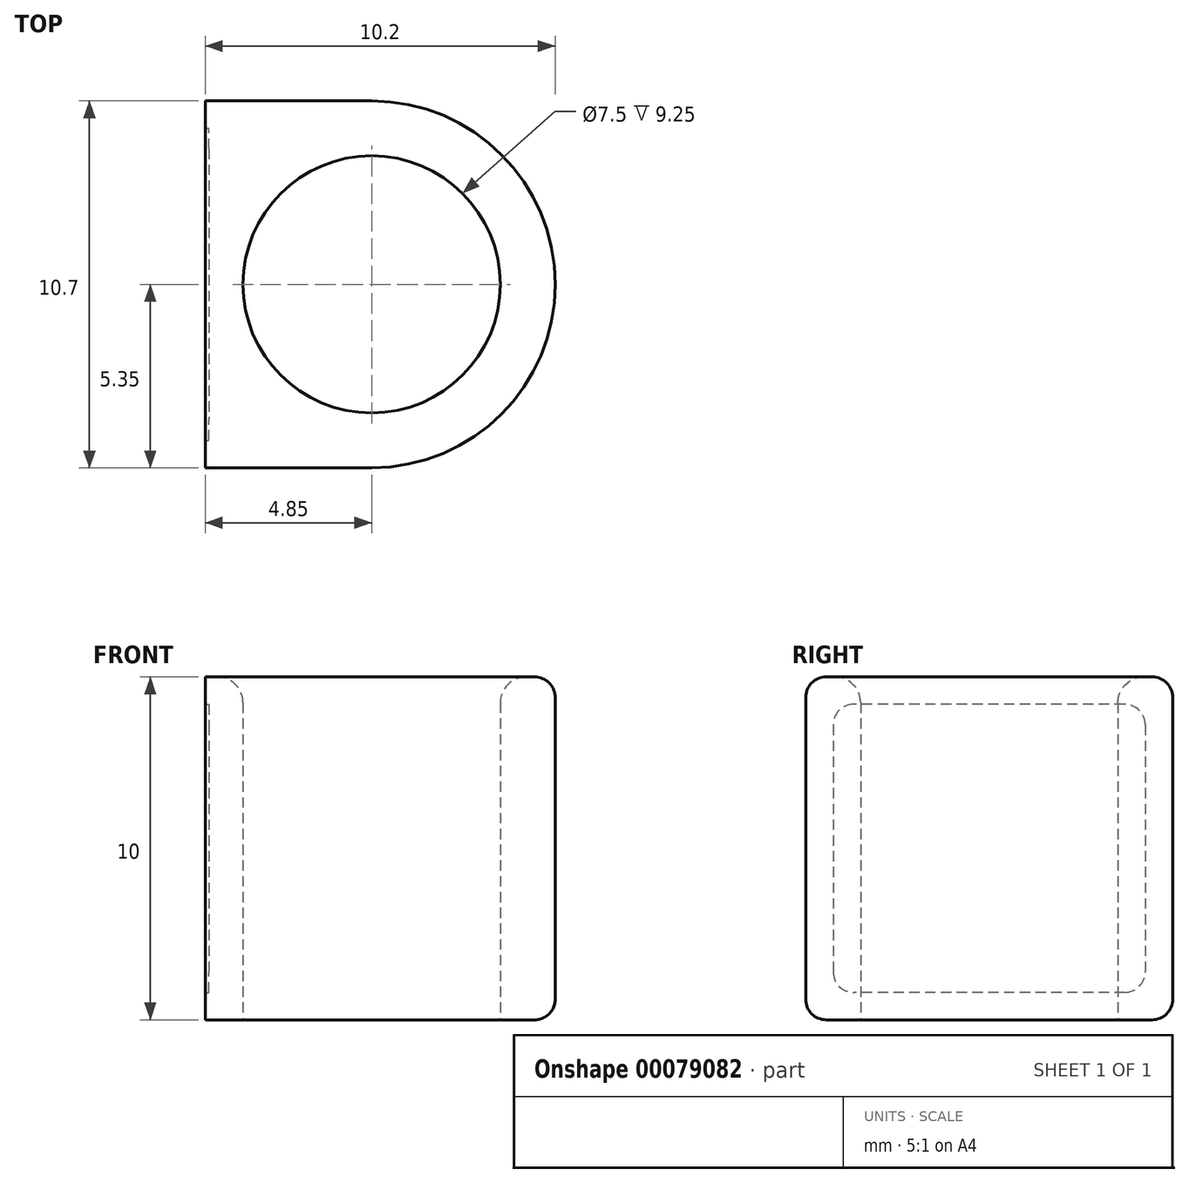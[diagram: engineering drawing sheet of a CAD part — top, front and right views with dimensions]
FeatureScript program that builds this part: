
annotation { "Feature Type Name" : "Feature", "Feature Type Description" : "" }
export const myFeature = defineFeature(function(context is Context, id is Id, definition is map)
    precondition{}
    {
        {
            var Q0;
            Q0=qCreatedBy(makeId("Top.planeOp"),FACE);
            var sketch = newSketch(context, id + "F0", { "sketchPlane" : qUnion([Q0])});
            skCircle(sketch, "E0", {"center": v(0, 0) * mm, "radius": 3.75 * mm});
            skCircle(sketch, "E1", {"center": v(0, 0) * mm, "radius": 5.35 * mm});
            skSolve(sketch);
        }
        {
            var Q0;
            Q0=makeQuery(id+"F0.imprint","IMPRINT",FACE,{"disambiguationData":[TD([[makeQuery(id+"F0.imprint","IMPRINT",EDGE,{"derivedFrom":sQuery(id+"F0.wireOp",EDGE,"E0")}),-1.0]])]});
            var Q1;
            Q1=makeQuery(id+"F0.imprint","IMPRINT",FACE,{"disambiguationData":[TD([[makeQuery(id+"F0.imprint","IMPRINT",EDGE,{"derivedFrom":sQuery(id+"F0.wireOp",EDGE,"E0")}),1.0]])]});
            extrude(context, id + "F1", {"entities" : qUnion([Q0, Q1]), "depth" : 10 * mm});
        }
        {
            var Q0;
            Q0=qCreatedBy(makeId("Right.planeOp"),FACE);
            var sketch = newSketch(context, id + "F2", { "sketchPlane" : qUnion([Q0])});
            skLineSegment(sketch, "E2.bottom", {"start": v(5.35, 10) * mm, "end": v(-5.35, 10) * mm});
            skLineSegment(sketch, "E2.top", {"start": v(5.35, 0) * mm, "end": v(-5.35, 0) * mm});
            skLineSegment(sketch, "E2.left", {"start": v(5.35, 10) * mm, "end": v(5.35, 0) * mm});
            skLineSegment(sketch, "E2.right", {"start": v(-5.35, 10) * mm, "end": v(-5.35, 0) * mm});
            skSolve(sketch);
        }
        {
            var Q0;
            Q0 = qSketchRegion(id + "F2", true);
            var Q1;
            Q1 = qConstructionFilter(qBodyType(qCreatedBy(id + "F2" ,EDGE), BodyType.WIRE), ConstructionObject.NO);
            extrude(context, id + "F3", {"entities" : qUnion([Q0]), "operationType" : NewBodyOperationType.ADD, "surfaceEntities" : qUnion([Q1]), "oppositeDirection" : true, "depth" : 4.75 * mm});
        }
        {
            var Q0;
            {var subQ1=sQuery(id+"F2.wireOp",EDGE,"E2.bottom");var subQ2=sQuery(id+"F2.wireOp",EDGE,"E2.top");var subQ3=sQuery(id+"F2.wireOp",EDGE,"E2.left");Q0=makeQuery(id+"F3.boolean.opBoolean","SPLIT",FACE,{"disambiguationData":[TD([makeQuery(id+"F3.opExtrude","SWEPT_FACE",FACE,{"disambiguationData":[OSD([subQ3])]})])],"derivedFrom":makeQuery(id+"F3.opExtrude","CAP_FACE",FACE,{"disambiguationData":[OSD([subQ1,subQ2,subQ3,sQuery(id+"F2.wireOp",EDGE,"E2.right")])],"isStart":false})});}
            var sketch = newSketch(context, id + "F4", { "sketchPlane" : qUnion([Q0])});
            skLineSegment(sketch, "E3.bottom", {"start": v(-5.35, 0) * mm, "end": v(5.35, 0) * mm});
            skLineSegment(sketch, "E3.top", {"start": v(-5.35, 10) * mm, "end": v(5.35, 10) * mm});
            skLineSegment(sketch, "E3.left", {"start": v(-5.35, 0) * mm, "end": v(-5.35, 10) * mm});
            skLineSegment(sketch, "E3.right", {"start": v(5.35, 0) * mm, "end": v(5.35, 10) * mm});
            skSolve(sketch);
        }
        {
            var Q0;
            {var subQ2=sQuery(id+"F4.wireOp",EDGE,"E3.right");Q0=makeQuery(id+"F4.imprint","IMPRINT",FACE,{"disambiguationData":[TD([[makeQuery(id+"F4.imprint","IMPRINT",EDGE,{"derivedFrom":subQ2}),1.0]])]});}
            extrude(context, id + "F5", {"entities" : qUnion([Q0]), "operationType" : NewBodyOperationType.REMOVE, "depth" : 25 * mm});
        }
        {
            var Q0;
            Q0=makeQuery(id+"F0.imprint","IMPRINT",FACE,{"disambiguationData":[TD([[makeQuery(id+"F0.imprint","IMPRINT",EDGE,{"derivedFrom":sQuery(id+"F0.wireOp",EDGE,"E0")}),1.0]])]});
            extrude(context, id + "F6", {"entities" : qUnion([Q0]), "operationType" : NewBodyOperationType.REMOVE, "depth" : 25 * mm});
        }
        {
            var Q0;
            Q0=makeQuery(id+"F3.opExtrude","CAP_FACE",FACE,{"disambiguationData":[OSD([sQuery(id+"F2.wireOp",EDGE,"E2.bottom"),sQuery(id+"F2.wireOp",EDGE,"E2.top"),sQuery(id+"F2.wireOp",EDGE,"E2.left"),sQuery(id+"F2.wireOp",EDGE,"E2.right")])],"isStart":false});
            var sketch = newSketch(context, id + "F7", { "sketchPlane" : qUnion([Q0])});
            skLineSegment(sketch, "E4.0", {"start": v(-4.55, 9.2) * mm, "end": v(-4.55, 0.8) * mm});
            skLineSegment(sketch, "E4.1", {"start": v(-4.55, 9.2) * mm, "end": v(4.55, 9.2) * mm});
            skLineSegment(sketch, "E4.2", {"start": v(4.55, 9.2) * mm, "end": v(4.55, 0.8) * mm});
            skLineSegment(sketch, "E4.3", {"start": v(-4.55, 0.8) * mm, "end": v(4.55, 0.8) * mm});
            skSolve(sketch);
        }
        {
            var Q0;
            Q0=makeQuery(id+"F7.imprint","IMPRINT",FACE,{"disambiguationData":[TD([[makeQuery(id+"F7.imprint","IMPRINT",EDGE,{"derivedFrom":sQuery(id+"F7.wireOp",EDGE,"E4.0")}),-1.0]])]});
            extrude(context, id + "F8", {"entities" : qUnion([Q0]), "operationType" : NewBodyOperationType.ADD, "depth" : 0.1 * mm});
        }
        {
            var Q0;
            {var subQ0=sQuery(id+"F2.wireOp",EDGE,"E2.left");var subQ1=sQuery(id+"F2.wireOp",EDGE,"E2.bottom");Q0=makeQuery(id+"F8.boolean.opBoolean","MERGE",EDGE,{"derivedFrom":[makeQuery(id+"F3.opExtrude","SWEPT_EDGE",EDGE,{"disambiguationData":[OSD([subQ1,subQ0])]}),makeQuery(id+"F8.opExtrude","SWEPT_EDGE",EDGE,{"disambiguationData":[OSD([subQ1,subQ0,sQuery(id+"F4.wireOp",EDGE,"E3.top")])]})]});}
            var Q1;
            {var subQ0=sQuery(id+"F2.wireOp",EDGE,"E2.left");var subQ1=sQuery(id+"F2.wireOp",EDGE,"E2.top");Q1=makeQuery(id+"F8.boolean.opBoolean","MERGE",EDGE,{"derivedFrom":[makeQuery(id+"F3.opExtrude","SWEPT_EDGE",EDGE,{"disambiguationData":[OSD([subQ1,subQ0])]}),makeQuery(id+"F8.opExtrude","SWEPT_EDGE",EDGE,{"disambiguationData":[OSD([subQ1,subQ0,sQuery(id+"F4.wireOp",EDGE,"E3.bottom")])]})]});}
            var Q2;
            {var subQ0=sQuery(id+"F2.wireOp",EDGE,"E2.right");var subQ1=sQuery(id+"F2.wireOp",EDGE,"E2.top");Q2=makeQuery(id+"F8.boolean.opBoolean","MERGE",EDGE,{"derivedFrom":[makeQuery(id+"F3.opExtrude","SWEPT_EDGE",EDGE,{"disambiguationData":[OSD([subQ1,subQ0])]}),makeQuery(id+"F8.opExtrude","SWEPT_EDGE",EDGE,{"disambiguationData":[OSD([subQ1,subQ0,sQuery(id+"F4.wireOp",EDGE,"E3.bottom")])]})]});}
            var Q3;
            {var subQ0=sQuery(id+"F2.wireOp",EDGE,"E2.right");var subQ1=sQuery(id+"F2.wireOp",EDGE,"E2.bottom");Q3=makeQuery(id+"F8.boolean.opBoolean","MERGE",EDGE,{"derivedFrom":[makeQuery(id+"F3.opExtrude","SWEPT_EDGE",EDGE,{"disambiguationData":[OSD([subQ1,subQ0])]}),makeQuery(id+"F8.opExtrude","SWEPT_EDGE",EDGE,{"disambiguationData":[OSD([subQ1,subQ0,sQuery(id+"F4.wireOp",EDGE,"E3.top")])]})]});}
            var Q4;
            Q4=makeQuery(id+"F8.opExtrude","SWEPT_EDGE",EDGE,{"disambiguationData":[OSD([sQuery(id+"F7.wireOp",EDGE,"E4.0"),sQuery(id+"F7.wireOp",EDGE,"E4.1")])]});
            var Q5;
            Q5=makeQuery(id+"F8.opExtrude","SWEPT_EDGE",EDGE,{"disambiguationData":[OSD([sQuery(id+"F7.wireOp",EDGE,"E4.1"),sQuery(id+"F7.wireOp",EDGE,"E4.2")])]});
            var Q6;
            Q6=makeQuery(id+"F8.opExtrude","SWEPT_EDGE",EDGE,{"disambiguationData":[OSD([sQuery(id+"F7.wireOp",EDGE,"E4.2"),sQuery(id+"F7.wireOp",EDGE,"E4.3")])]});
            var Q7;
            Q7=makeQuery(id+"F8.opExtrude","SWEPT_EDGE",EDGE,{"disambiguationData":[OSD([sQuery(id+"F7.wireOp",EDGE,"E4.0"),sQuery(id+"F7.wireOp",EDGE,"E4.3")])]});
            fillet(context, id + "F9", {"entities" : qUnion([Q0, Q1, Q2, Q3, Q4, Q5, Q6, Q7]), "radius" : 0.6 * mm, "tangentPropagation" : true, "allowEdgeOverflow" : false});
        }
        {
            var Q0;
            Q0=makeQuery(id+"F6.boolean.opBoolean","COPY",EDGE,{"derivedFrom":makeQuery(id+"F6.opExtrude","CAP_EDGE",EDGE,{"disambiguationData":[OSD([sQuery(id+"F0.wireOp",EDGE,"E0")])],"isStart":true})});
            var Q1;
            Q1=makeQuery(id+"F6.boolean.opBoolean","INTERSECT",EDGE,{"derivedFrom":[makeQuery(id+"F3.boolean.opBoolean","MERGE",FACE,{"derivedFrom":[makeQuery(id+"F1.opExtrude","CAP_FACE",FACE,{"disambiguationData":[OSD([sQuery(id+"F0.wireOp",EDGE,"E1")])],"isStart":false}),makeQuery(id+"F3.opExtrude","SWEPT_FACE",FACE,{"disambiguationData":[OSD([sQuery(id+"F2.wireOp",EDGE,"E2.bottom")])]})]}),makeQuery(id+"F6.opExtrude","SWEPT_FACE",FACE,{"disambiguationData":[OSD([sQuery(id+"F0.wireOp",EDGE,"E0")])]})]});
            fillet(context, id + "F10", {"entities" : qUnion([Q0, Q1]), "radius" : 0.75 * mm, "tangentPropagation" : true, "allowEdgeOverflow" : false});
        }
    });
